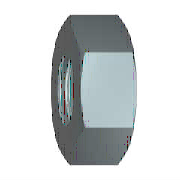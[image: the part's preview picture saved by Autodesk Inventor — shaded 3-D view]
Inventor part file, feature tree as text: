
AUTODESK INVENTOR PART (.ipt)
format: ipt  version: 2013 (Build 170138000, 138)  size: 173,056 bytes
history: native  units: mm (DEFAULTED — no unit token found)
features: sketch x3, chamfer x1, hole x1, other x1, plane x1
ambient origin geometry x7: Origin, YZ Plane, XZ Plane, X Axis, Y Axis, Z Axis, Center Point
bodies: Solid1 (feature_tree), Body (feature_tree)
feature tree (7):
  chamfer  "Chamfer1"  Distance=4.363323mm
  hole  "Thread"  [1 undecoded]
  other  "Work Axis1"
  plane  "Work Plane1"
  sketch  "Sketch1"  dims[d0=15.011107mm]
  sketch  "Sketch2"  dims[d1=6.8mm]
  sketch  "Sketch3"  dims[d2=0.0mm d3=4.363323mm d4=4.363323mm d5=13.0mm d6=13.0mm d7=90.0deg d25=6.647mm d26=6.0mm d27=4.0mm d28=2.0mm d29=14.3117mm d30=8.0mm d31=20.594885mm d8=0.676582mm d9=30.0deg d10=0.676582mm d11=30.0deg d13=0.0mm d14=0.0mm d39=0.0mm d40=0.676582mm d41=0.676582mm d42=0.0mm]
note: 1 required parameter value undecoded (feature->parameter linkage not recoverable at this tier; creation-order binding heuristic only, values carry confidence <= 0.55)
